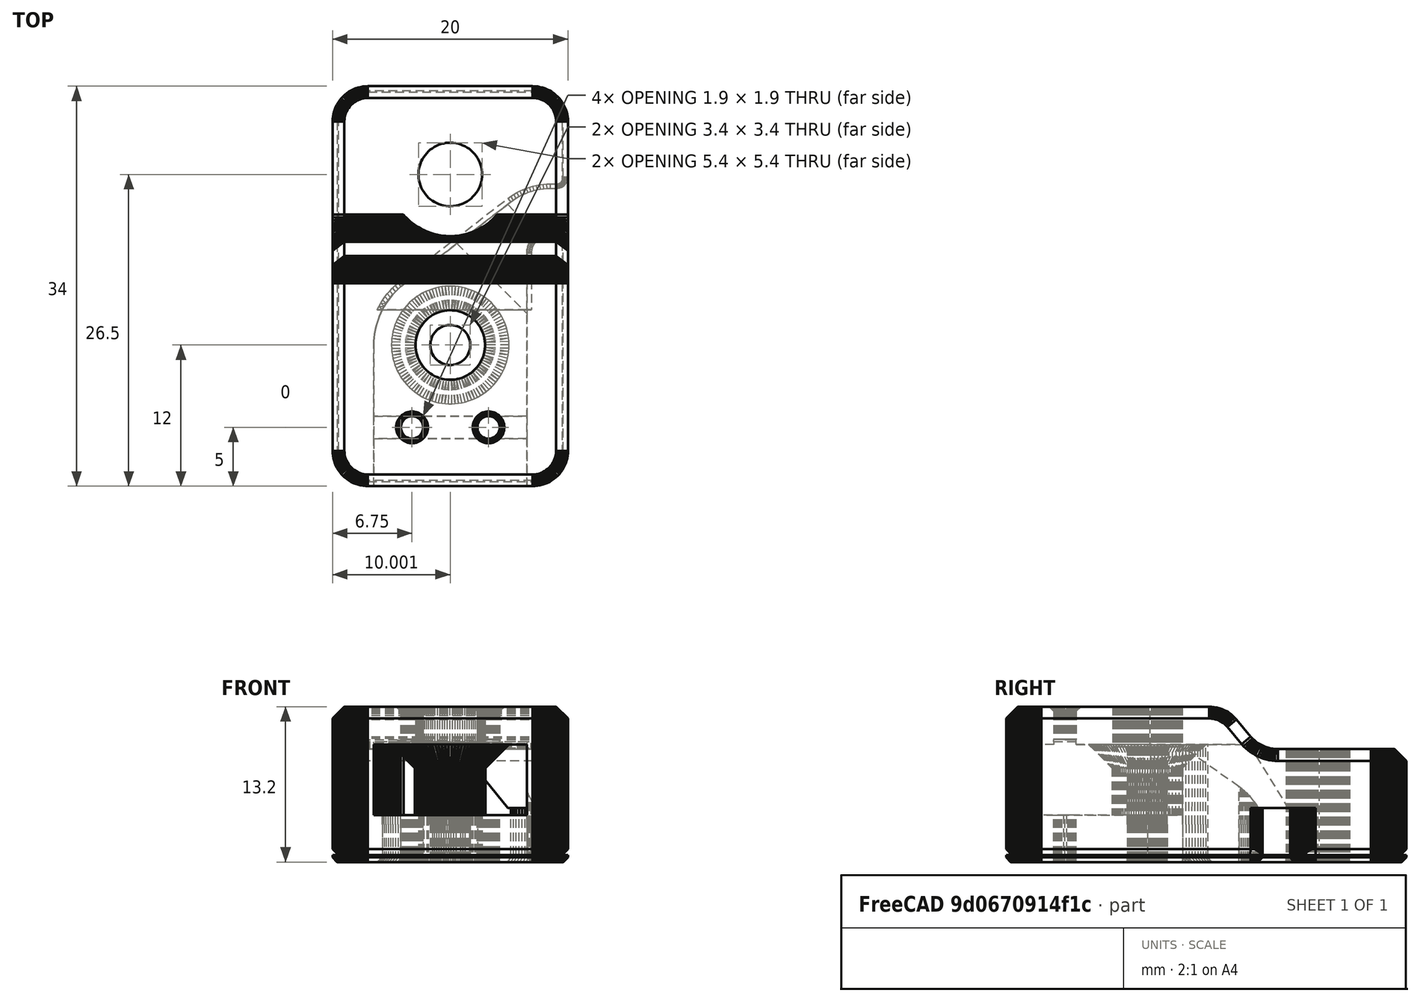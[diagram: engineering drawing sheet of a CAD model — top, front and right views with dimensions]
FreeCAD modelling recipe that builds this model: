
FCSTD DOCUMENT  (FreeCAD 1.0R39109 (Git))
Label: Endstop_Y_housing
License: All rights reserved
LicenseURL: https://en.wikipedia.org/wiki/All_rights_reserved
objects: Part::FeaturePython×3, Part::Feature×1, Part::Refine×1, Part::Plane×1, App::DocumentObjectGroup×1, PartDesign::FeatureBase×1, PartDesign::Pad×1, PartDesign::Chamfer×1, PartDesign::Body×1
note: 15 computed .brp shape members not serialized (recipe doc carries the construction recipe); baked Part::Feature solids carry a one-line shape summary decoded from their .brp

FEATURE [Part::Feature] _a__y_endstop_housing001_solid  label="_a__y_endstop_housing001 (Solid)"
  shape: bbox 20 x 34 x 10.6 mm, 4684 faces (baked)
FEATURE [Part::Refine] _a__y_endstop_housing001_solid001  label="_a__y_endstop_housing001 (Solid)001"
  Source = -> _a__y_endstop_housing001_solid
FEATURE [Part::Plane] Plane
  AttacherType = Attacher::AttachEngine3D
  Length = 100
  Placement = pos=(-50,-50,0) rot=(0,0,1;0rad)
  Width = 100
FEATURE [Part::FeaturePython] Slice  # WARN: FeaturePython — macro-defined, semantics opaque (R4)
  Base = -> _a__y_endstop_housing001_solid001
  Mode = 1
  Tolerance = 0
  Tools = -> [Plane]
FEATURE [Part::FeaturePython] Slice_child0  label="Slice.0"  # WARN: FeaturePython — macro-defined, semantics opaque (R4)
  Base = -> Slice
  FilterType = 1
  Invert = false
  OverrideMaxVal = 0
  Placement = pos=(0,0,2) rot=(0,0,1;0rad)
  WindowFrom = 80
  WindowTo = 100
  items = 0
FEATURE [Part::FeaturePython] Slice_child1  label="Slice.1"  # WARN: FeaturePython — macro-defined, semantics opaque (R4)
  Base = -> Slice
  FilterType = 1
  Invert = false
  OverrideMaxVal = 0
  WindowFrom = 80
  WindowTo = 100
  items = 1
FEATURE [App::DocumentObjectGroup] GrExplode_Slice  label="Exploded Slice"
  Group = -> [Slice_child0,Slice_child1]
FEATURE [PartDesign::FeatureBase] BaseFeature
  BaseFeature = -> Slice_child0
  Suppressed = false
FEATURE [PartDesign::Pad] Pad
  BaseFeature = -> BaseFeature
  Direction = (0,0,-1)
  Length = 2.6
  Length2 = 10
  Profile = -> BaseFeature [Face5]
  Refine = true
  Suppressed = false
  Type = 0
FEATURE [PartDesign::Chamfer] Chamfer
  Angle = 45
  Base = -> Pad [Edge358]
  BaseFeature = -> Pad
  ChamferType = 0
  FlipDirection = false
  Refine = true
  Size = 0.5
  Size2 = 1
  SupportTransform = false
  Suppressed = false
  UseAllEdges = false
FEATURE [PartDesign::Body] Body
  AllowCompound = false
  BaseFeature = -> Slice_child0
  Group = -> [BaseFeature,Pad,Chamfer]
  Origin = -> Origin
  Placement = pos=(0,0,2.6) rot=(0,0,1;0rad)
  Tip = -> Chamfer
